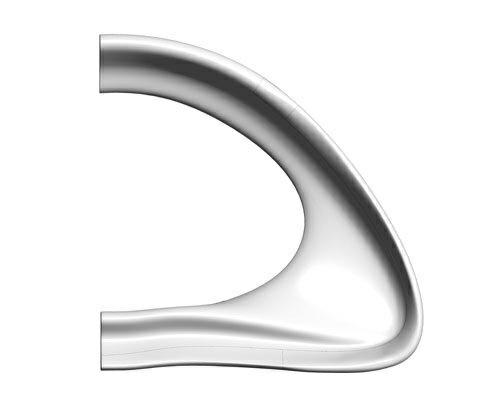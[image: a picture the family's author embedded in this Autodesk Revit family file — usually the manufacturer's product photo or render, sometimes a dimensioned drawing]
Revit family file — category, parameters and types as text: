
# Revit family: CITY ALPHABET letter „V” vertical
name_source: partatom
category: Furniture
revit_build: Autodesk Revit 2018 (Build: 20190510_1515(x64)
units: mm (PartAtom-declared; Revit-internal decimal feet)

## family parameters
Cut with Voids When Loaded = No
Host = Face
OmniClass Number = 23.40.10.11.14
OmniClass Title = Exterior Seating
Room Calculation Point = No
Shared = No

## types (1)
- CITY ALPHABET letter „V”
    Default Elevation = 1219 mm
    Height = 1900 mm  [stored 6.2336 ft]
    IfcExportAs = IfcFurnishingElement
    Length = 1850 mm  [stored 6.06955 ft]
    Manufacturer = Astrini Design
    Material information = Colour choice from RAL colour standard. Customer may inquire about specific request regarding individual order.
    Model = CITY ALPHABET letter „V”
    Operating temperature = -40°C to 80°C, ( -40°F to 176°F )
    Type Comments = Bench
    Type Image = V.jpg
    URL = https://astrini-design.pl
    Weight (approximately) = 80.00 kg
    Weight - filled (approximately) = 130.00 kg
    Width = 850 mm  [stored 2.78871 ft]

note: [stored X ft] marks values corroborated as IEEE doubles in the binary element streams (Revit-internal decimal feet)
